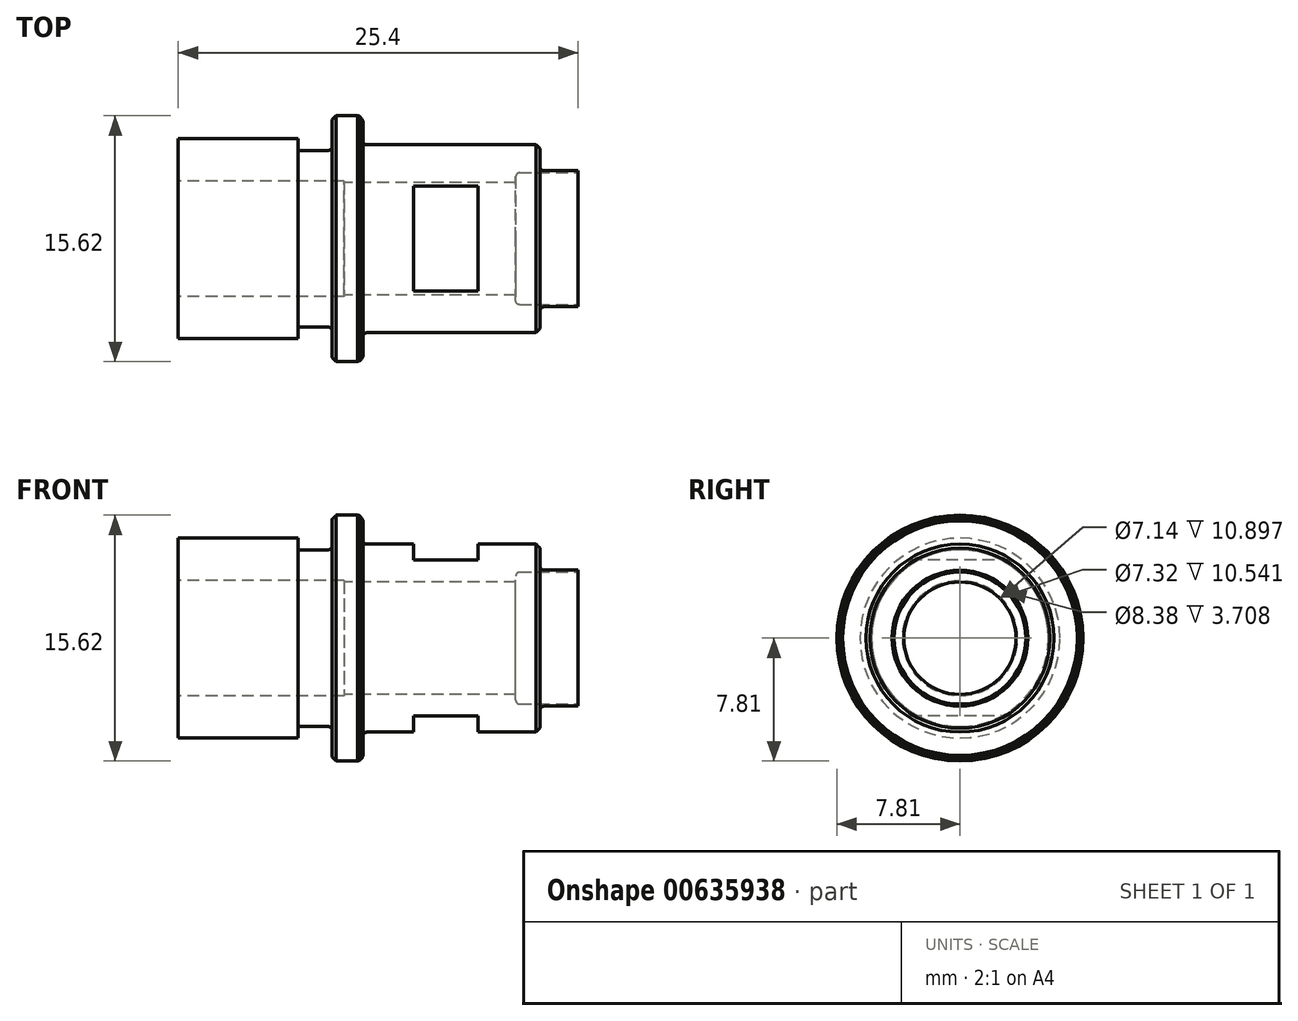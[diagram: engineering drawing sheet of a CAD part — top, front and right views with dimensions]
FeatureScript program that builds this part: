
annotation { "Feature Type Name" : "Feature", "Feature Type Description" : "" }
export const myFeature = defineFeature(function(context is Context, id is Id, definition is map)
    precondition{}
    {
        {
            var Q0;
            Q0=qCreatedBy(makeId("Front.planeOp"),FACE);
            var sketch = newSketch(context, id + "F0", { "sketchPlane" : qUnion([Q0])});
            skLineSegment(sketch, "E0", {"start": v(-15.23, 0) * mm, "end": v(29.04, 0) * mm, "construction": true});
            skLineSegment(sketch, "E1", {"start": v(0, 3.57) * mm, "end": v(25.4, 3.57) * mm});
            skLineSegment(sketch, "E2", {"start": v(0, 6.35) * mm, "end": v(25.4, 6.35) * mm});
            skLineSegment(sketch, "E3", {"start": v(25.4, 3.57) * mm, "end": v(25.4, 6.35) * mm});
            skLineSegment(sketch, "E4", {"start": v(0, 3.57) * mm, "end": v(0, 6.35) * mm});
            skSolve(sketch);
        }
        {
            var Q0;
            Q0 = qSketchRegion(id + "F0", true);
            var Q1;
            Q1=sQuery(id+"F0.wireOp",EDGE,"E0");
            revolve(context, id + "F1", {"entities" : qUnion([Q0]), "axis" : qUnion([Q1]), "revolveType" : RevolveType.FULL});
        }
        {
            var Q0;
            Q0=qCreatedBy(makeId("Front.planeOp"),FACE);
            var sketch = newSketch(context, id + "F2", { "sketchPlane" : qUnion([Q0])});
            skLineSegment(sketch, "E5", {"start": v(-9.32, 0) * mm, "end": v(34, 0) * mm, "construction": true});
            skLineSegment(sketch, "E6", {"start": v(9.78, 6.35) * mm, "end": v(9.78, 7.81) * mm});
            skLineSegment(sketch, "E7", {"start": v(9.78, 7.81) * mm, "end": v(11.73, 7.81) * mm});
            skLineSegment(sketch, "E8", {"start": v(11.73, 7.81) * mm, "end": v(11.73, 6.35) * mm});
            skLineSegment(sketch, "E9", {"start": v(9.78, 6.35) * mm, "end": v(11.73, 6.35) * mm});
            skSolve(sketch);
        }
        {
            var Q0;
            Q0 = qSketchRegion(id + "F2", true);
            var Q1;
            Q1=sQuery(id+"F2.wireOp",EDGE,"E5");
            revolve(context, id + "F3", {"operationType" : NewBodyOperationType.ADD, "entities" : qUnion([Q0]), "axis" : qUnion([Q1]), "revolveType" : RevolveType.FULL});
        }
        {
            var Q0;
            Q0=qCreatedBy(makeId("Front.planeOp"),FACE);
            var sketch = newSketch(context, id + "F4", { "sketchPlane" : qUnion([Q0])});
            skLineSegment(sketch, "E10", {"start": v(-6.28, 0) * mm, "end": v(38.7, 0) * mm, "construction": true});
            skLineSegment(sketch, "E11", {"start": v(11.73, 8.9) * mm, "end": v(25.4, 8.9) * mm});
            skLineSegment(sketch, "E12", {"start": v(25.4, 8.9) * mm, "end": v(25.4, 5.97) * mm});
            skLineSegment(sketch, "E13", {"start": v(25.4, 5.97) * mm, "end": v(11.73, 5.97) * mm});
            skLineSegment(sketch, "E14", {"start": v(11.73, 5.97) * mm, "end": v(11.73, 8.89) * mm});
            skSolve(sketch);
        }
        {
            var Q0;
            Q0 = qSketchRegion(id + "F4", true);
            var Q1;
            Q1=sQuery(id+"F4.wireOp",EDGE,"E10");
            revolve(context, id + "F5", {"operationType" : NewBodyOperationType.REMOVE, "entities" : qUnion([Q0]), "axis" : qUnion([Q1]), "revolveType" : RevolveType.FULL, "oppositeDirection" : true});
        }
        {
            var Q0;
            Q0=qCreatedBy(makeId("Front.planeOp"),FACE);
            var sketch = newSketch(context, id + "F6", { "sketchPlane" : qUnion([Q0])});
            skLineSegment(sketch, "E15", {"start": v(7.62, 8.9) * mm, "end": v(7.62, 5.61) * mm});
            skLineSegment(sketch, "E16", {"start": v(7.62, 5.61) * mm, "end": v(9.78, 5.61) * mm});
            skLineSegment(sketch, "E17", {"start": v(9.78, 5.61) * mm, "end": v(9.78, 8.89) * mm});
            skLineSegment(sketch, "E18", {"start": v(9.78, 8.9) * mm, "end": v(7.62, 8.9) * mm});
            skLineSegment(sketch, "E19", {"start": v(-1.06, 0) * mm, "end": v(16.03, 0) * mm, "construction": true});
            skLineSegment(sketch, "E20", {"start": v(22.99, 8.9) * mm, "end": v(22.99, 4.32) * mm});
            skLineSegment(sketch, "E21", {"start": v(22.99, 4.32) * mm, "end": v(25.4, 4.32) * mm});
            skLineSegment(sketch, "E22", {"start": v(25.4, 4.32) * mm, "end": v(25.4, 8.9) * mm});
            skLineSegment(sketch, "E23", {"start": v(25.4, 8.9) * mm, "end": v(22.99, 8.9) * mm});
            skSolve(sketch);
        }
        {
            var Q0;
            Q0 = qSketchRegion(id + "F6", true);
            var Q1;
            Q1=sQuery(id+"F6.wireOp",EDGE,"E19");
            revolve(context, id + "F7", {"operationType" : NewBodyOperationType.REMOVE, "entities" : qUnion([Q0]), "axis" : qUnion([Q1]), "revolveType" : RevolveType.FULL, "oppositeDirection" : true});
        }
        {
            var Q0;
            Q0=makeQuery(id+"F1.opRevolve","SWEPT_FACE",FACE,{"disambiguationData":[OSD([sQuery(id+"F0.wireOp",EDGE,"E4")])]});
            var sketch = newSketch(context, id + "F8", { "sketchPlane" : qUnion([Q0])});
            skCircle(sketch, "E24", {"center": v(0, 0) * mm, "radius": 3.66 * mm});
            skSolve(sketch);
        }
        {
            var Q0;
            Q0 = qSketchRegion(id + "F8", true);
            extrude(context, id + "F9", {"entities" : qUnion([Q0]), "operationType" : NewBodyOperationType.REMOVE, "oppositeDirection" : true, "depth" : 10.54 * mm, "offsetDistance" : 25.4 * mm});
        }
        {
            var Q0;
            Q0=makeQuery(id+"F1.opRevolve","SWEPT_FACE",FACE,{"disambiguationData":[OSD([sQuery(id+"F0.wireOp",EDGE,"E3")])]});
            var sketch = newSketch(context, id + "F10", { "sketchPlane" : qUnion([Q0])});
            skCircle(sketch, "E25", {"center": v(0, 0) * mm, "radius": 4.2 * mm});
            skSolve(sketch);
        }
        {
            var Q0;
            Q0 = qSketchRegion(id + "F10", true);
            extrude(context, id + "F11", {"entities" : qUnion([Q0]), "operationType" : NewBodyOperationType.REMOVE, "oppositeDirection" : true, "depth" : 3.96 * mm, "offsetDistance" : 25.4 * mm});
        }
        {
            var Q0;
            Q0=qCreatedBy(makeId("Front.planeOp"),FACE);
            var sketch = newSketch(context, id + "F12", { "sketchPlane" : qUnion([Q0])});
            skLineSegment(sketch, "E26", {"start": v(-5.92, 0) * mm, "end": v(32.5, 0) * mm, "construction": true});
            skLineSegment(sketch, "E27", {"start": v(14.94, 8.9) * mm, "end": v(14.94, 4.95) * mm});
            skLineSegment(sketch, "E28", {"start": v(14.94, 4.95) * mm, "end": v(19.05, 4.95) * mm});
            skLineSegment(sketch, "E29", {"start": v(19.05, 4.95) * mm, "end": v(19.05, 8.9) * mm});
            skLineSegment(sketch, "E30", {"start": v(19.05, 8.9) * mm, "end": v(14.94, 8.9) * mm});
            skLineSegment(sketch, "E31.MirrorCS", {"start": v(14.94, -8.9) * mm, "end": v(14.94, -4.95) * mm});
            skLineSegment(sketch, "E32.MirrorCS", {"start": v(14.94, -4.95) * mm, "end": v(19.05, -4.95) * mm});
            skLineSegment(sketch, "E33.MirrorCS", {"start": v(19.05, -4.95) * mm, "end": v(19.05, -8.9) * mm});
            skLineSegment(sketch, "E34.MirrorCS", {"start": v(19.05, -8.9) * mm, "end": v(14.94, -8.9) * mm});
            skSolve(sketch);
        }
        {
            var Q0;
            Q0 = qSketchRegion(id + "F12", true);
            extrude(context, id + "F13", {"entities" : qUnion([Q0]), "operationType" : NewBodyOperationType.REMOVE, "endBound" : BoundingType.THROUGH_ALL, "oppositeDirection" : true, "depth" : 25.4 * mm, "offsetDistance" : 25.4 * mm, "hasSecondDirection" : true, "secondDirectionBound" : SecondDirectionBoundingType.THROUGH_ALL, "secondDirectionOppositeDirection" : false, "secondDirectionDepth" : 25.4 * mm});
        }
        {
            var Q0;
            Q0=makeQuery(id+"F3.opRevolve","SWEPT_EDGE",EDGE,{"disambiguationData":[OSD([sQuery(id+"F2.wireOp",EDGE,"E6"),sQuery(id+"F2.wireOp",EDGE,"E7")])]});
            var Q1;
            Q1=makeQuery(id+"F3.opRevolve","SWEPT_EDGE",EDGE,{"disambiguationData":[OSD([sQuery(id+"F2.wireOp",EDGE,"E7"),sQuery(id+"F2.wireOp",EDGE,"E8")])]});
            chamfer(context, id + "F14", {"entities" : qUnion([Q0, Q1]), "width" : 0.25 * mm, "tangentPropagation" : true});
        }
        {
            var Q0;
            {var subQ0=sQuery(id+"F2.wireOp",EDGE,"E8");Q0=makeQuery(id+"F14.opChamfer","BLEND_EDGE",EDGE,{"blendedFrom":[makeQuery(id+"F3.opRevolve","SWEPT_EDGE",EDGE,{"disambiguationData":[OSD([sQuery(id+"F2.wireOp",EDGE,"E7"),subQ0])]}),makeQuery(id+"F5.boolean.opBoolean","MERGE",FACE,{"derivedFrom":[makeQuery(id+"F3.opRevolve","SWEPT_FACE",FACE,{"disambiguationData":[OSD([subQ0])]}),makeQuery(id+"F5.opRevolve","SWEPT_FACE",FACE,{"disambiguationData":[OSD([sQuery(id+"F4.wireOp",EDGE,"E14")])]})]})],"blendedInto":[makeQuery(id+"F5.boolean.opBoolean","MERGE",FACE,{"derivedFrom":[makeQuery(id+"F3.opRevolve","SWEPT_FACE",FACE,{"disambiguationData":[OSD([subQ0])]}),makeQuery(id+"F5.opRevolve","SWEPT_FACE",FACE,{"disambiguationData":[OSD([sQuery(id+"F4.wireOp",EDGE,"E14")])]})]})]});}
            var Q1;
            {var subQ0=sQuery(id+"F2.wireOp",EDGE,"E7");Q1=makeQuery(id+"F14.opChamfer","BLEND_EDGE",EDGE,{"blendedFrom":[makeQuery(id+"F3.opRevolve","SWEPT_EDGE",EDGE,{"disambiguationData":[OSD([subQ0,sQuery(id+"F2.wireOp",EDGE,"E8")])]}),makeQuery(id+"F3.opRevolve","SWEPT_FACE",FACE,{"disambiguationData":[OSD([subQ0])]})],"blendedInto":[makeQuery(id+"F3.opRevolve","SWEPT_FACE",FACE,{"disambiguationData":[OSD([subQ0])]})]});}
            chamfer(context, id + "F15", {"entities" : qUnion([Q0, Q1]), "width" : 0.25 * mm, "tangentPropagation" : true});
        }
        {
            var Q0;
            Q0=makeQuery(id+"F7.boolean.opBoolean","COPY",EDGE,{"derivedFrom":makeQuery(id+"F7.opRevolve","SWEPT_EDGE",EDGE,{"disambiguationData":[OSD([sQuery(id+"F6.wireOp",EDGE,"E16"),sQuery(id+"F6.wireOp",EDGE,"E17")])]})});
            var Q1;
            Q1=makeQuery(id+"F5.boolean.opBoolean","COPY",EDGE,{"derivedFrom":makeQuery(id+"F5.opRevolve","SWEPT_EDGE",EDGE,{"disambiguationData":[OSD([sQuery(id+"F4.wireOp",EDGE,"E13"),sQuery(id+"F4.wireOp",EDGE,"E14")])]})});
            var Q2;
            Q2=makeQuery(id+"F7.boolean.opBoolean","COPY",EDGE,{"derivedFrom":makeQuery(id+"F7.opRevolve","SWEPT_EDGE",EDGE,{"disambiguationData":[OSD([sQuery(id+"F6.wireOp",EDGE,"E20"),sQuery(id+"F6.wireOp",EDGE,"E21")])]})});
            var Q3;
            Q3=makeQuery(id+"F11.boolean.opBoolean","COPY",EDGE,{"derivedFrom":makeQuery(id+"F11.opExtrude","CAP_EDGE",EDGE,{"disambiguationData":[OSD([sQuery(id+"F10.wireOp",EDGE,"E25")])],"isStart":false})});
            fillet(context, id + "F16", {"entities" : qUnion([Q0, Q1, Q2, Q3]), "radius" : 0.25 * mm, "tangentPropagation" : true, "allowEdgeOverflow" : false});
        }
        {
            var Q0;
            Q0=makeQuery(id+"F7.boolean.opBoolean","INTERSECT",EDGE,{"derivedFrom":[makeQuery(id+"F5.boolean.opBoolean","COPY",FACE,{"derivedFrom":makeQuery(id+"F5.opRevolve","SWEPT_FACE",FACE,{"disambiguationData":[OSD([sQuery(id+"F4.wireOp",EDGE,"E13")])]})}),makeQuery(id+"F7.opRevolve","SWEPT_FACE",FACE,{"disambiguationData":[OSD([sQuery(id+"F6.wireOp",EDGE,"E20")])]})]});
            chamfer(context, id + "F17", {"entities" : qUnion([Q0]), "width" : 0.25 * mm, "tangentPropagation" : true});
        }
    });
